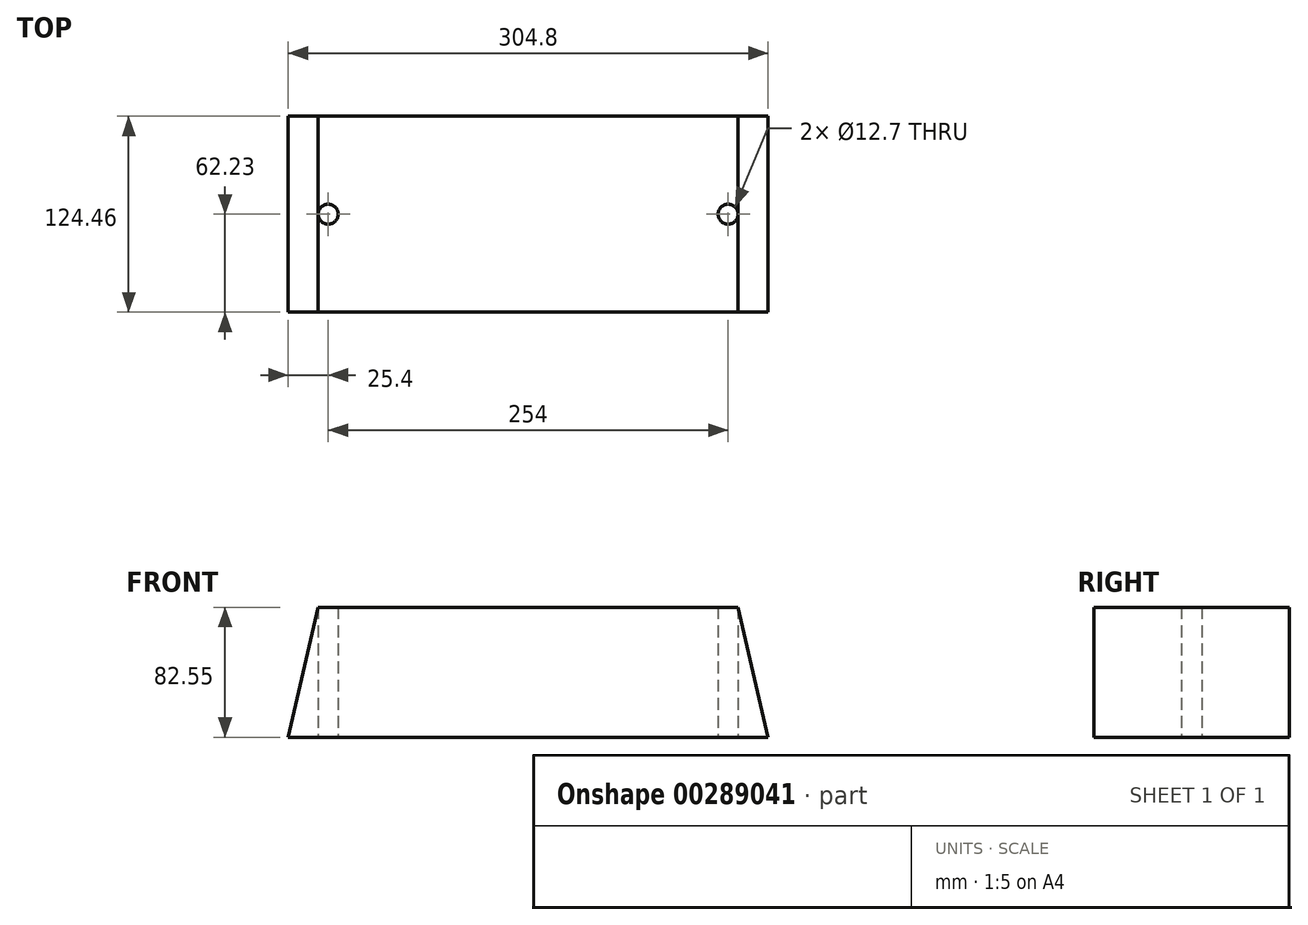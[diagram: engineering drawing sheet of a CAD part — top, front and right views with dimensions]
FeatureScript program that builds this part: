
annotation { "Feature Type Name" : "Feature", "Feature Type Description" : "" }
export const myFeature = defineFeature(function(context is Context, id is Id, definition is map)
    precondition{}
    {
        {
            var Q0;
            Q0=qCreatedBy(makeId("Front.planeOp"),FACE);
            var sketch = newSketch(context, id + "F0", { "sketchPlane" : qUnion([Q0])});
            skLineSegment(sketch, "E0", {"start": v(0, 0) * mm, "end": v(152.4, 0) * mm});
            skLineSegment(sketch, "E1", {"start": v(152.4, 0) * mm, "end": v(133.35, 82.55) * mm});
            skLineSegment(sketch, "E2", {"start": v(133.35, 82.55) * mm, "end": v(0, 82.55) * mm});
            skLineSegment(sketch, "E3", {"start": v(0, 82.55) * mm, "end": v(0, 0) * mm});
            skSolve(sketch);
        }
        {
            var Q0;
            Q0 = qSketchRegion(id + "F0", true);
            extrude(context, id + "F1", {"entities" : qUnion([Q0]), "endBound" : BoundingType.SYMMETRIC, "offsetDistance" : 25.4 * mm, "depth" : 124.46 * mm});
        }
        {
            var Q0;
            Q0=makeQuery(id+"F1.opExtrude","SWEPT_BODY",BODY,{"disambiguationData":[OSD([sQuery(id+"F0.wireOp",EDGE,"E0"),sQuery(id+"F0.wireOp",EDGE,"E1"),sQuery(id+"F0.wireOp",EDGE,"E2"),sQuery(id+"F0.wireOp",EDGE,"E3")])]});
            var Q1;
            Q1=qCreatedBy(makeId("Right.planeOp"),FACE);
            mirror(context, id + "F2", {"operationType" : NewBodyOperationType.ADD, "entities" : qUnion([Q0]), "mirrorPlane" : qUnion([Q1])});
        }
        {
            var Q0;
            {var subQ0=makeQuery(id+"F1.opExtrude","SWEPT_FACE",FACE,{"disambiguationData":[OSD([sQuery(id+"F0.wireOp",EDGE,"E0")])]});Q0=makeQuery(id+"F2.boolean.opBoolean","MERGE",FACE,{"derivedFrom":[subQ0,makeQuery(id+"F2.opPattern","COPY",FACE,{"derivedFrom":subQ0,"instanceName":"1"})]});}
            var sketch = newSketch(context, id + "F3", { "sketchPlane" : qUnion([Q0])});
            skLineSegment(sketch, "E4", {"start": v(152.4, 0) * mm, "end": v(-152.4, 0) * mm, "construction": true});
            skCircle(sketch, "E5", {"center": v(127, 0) * mm, "radius": 6.35 * mm});
            skCircle(sketch, "E6", {"center": v(-127, 0) * mm, "radius": 6.35 * mm});
            skLineSegment(sketch, "E7", {"start": v(0, -62.23) * mm, "end": v(0, 62.23) * mm, "construction": true});
            skSolve(sketch);
        }
        {
            var Q0;
            Q0 = qSketchRegion(id + "F3", true);
            extrude(context, id + "F4", {"entities" : qUnion([Q0]), "operationType" : NewBodyOperationType.REMOVE, "endBound" : BoundingType.THROUGH_ALL, "oppositeDirection" : true, "depth" : 25.4 * mm});
        }
    });
